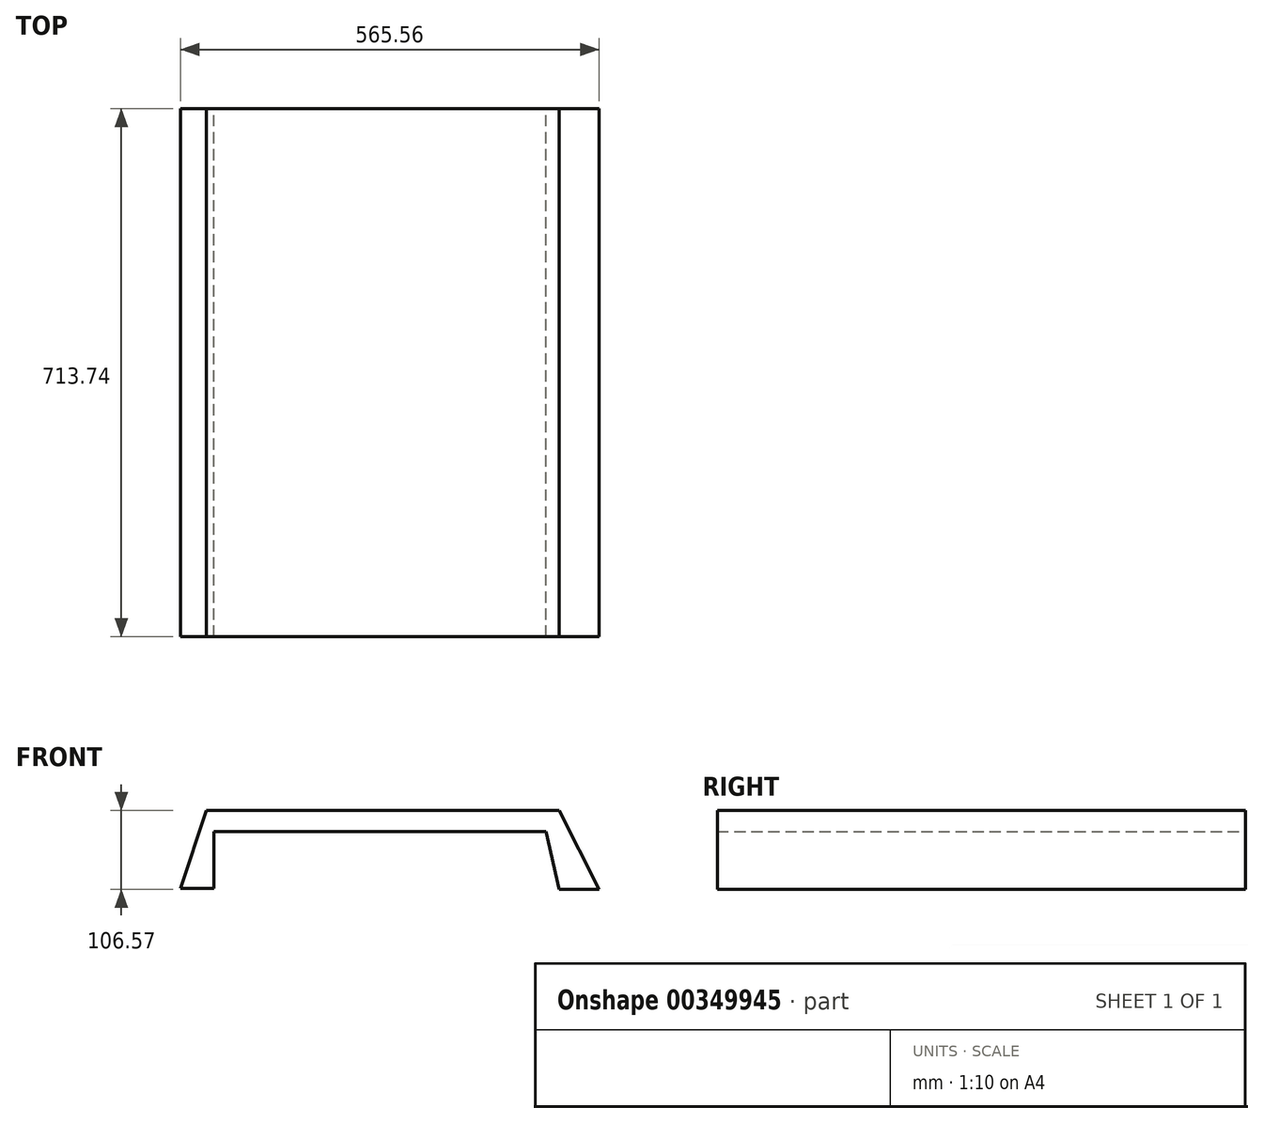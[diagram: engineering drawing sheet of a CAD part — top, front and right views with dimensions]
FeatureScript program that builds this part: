
annotation { "Feature Type Name" : "Feature", "Feature Type Description" : "" }
export const myFeature = defineFeature(function(context is Context, id is Id, definition is map)
    precondition{}
    {
        {
            var Q0;
            Q0=qCreatedBy(makeId("Front.planeOp"),FACE);
            var sketch = newSketch(context, id + "F0", { "sketchPlane" : qUnion([Q0])});
            skLineSegment(sketch, "E0", {"start": v(-189.88, 276.6) * mm, "end": v(287.07, 276.6) * mm});
            skLineSegment(sketch, "E1", {"start": v(269.13, 248.2) * mm, "end": v(-179.42, 248.2) * mm});
            skLineSegment(sketch, "E2", {"start": v(287.07, 276.6) * mm, "end": v(340.96, 170.03) * mm});
            skLineSegment(sketch, "E3", {"start": v(340.96, 170.03) * mm, "end": v(287.07, 170.03) * mm});
            skLineSegment(sketch, "E4", {"start": v(287.07, 170.03) * mm, "end": v(269.13, 248.2) * mm});
            skLineSegment(sketch, "E5", {"start": v(-189.88, 276.6) * mm, "end": v(-224.6, 171.06) * mm});
            skLineSegment(sketch, "E6", {"start": v(-224.6, 171.06) * mm, "end": v(-179.42, 171.06) * mm});
            skLineSegment(sketch, "E7", {"start": v(-179.42, 171.06) * mm, "end": v(-179.42, 248.2) * mm});
            skSolve(sketch);
        }
        {
            var Q0;
            Q0 = qSketchRegion(id + "F0", true);
            extrude(context, id + "F1", {"entities" : qUnion([Q0]), "depth" : 713.74 * mm, "offsetDistance" : 25.4 * mm});
        }
    });
